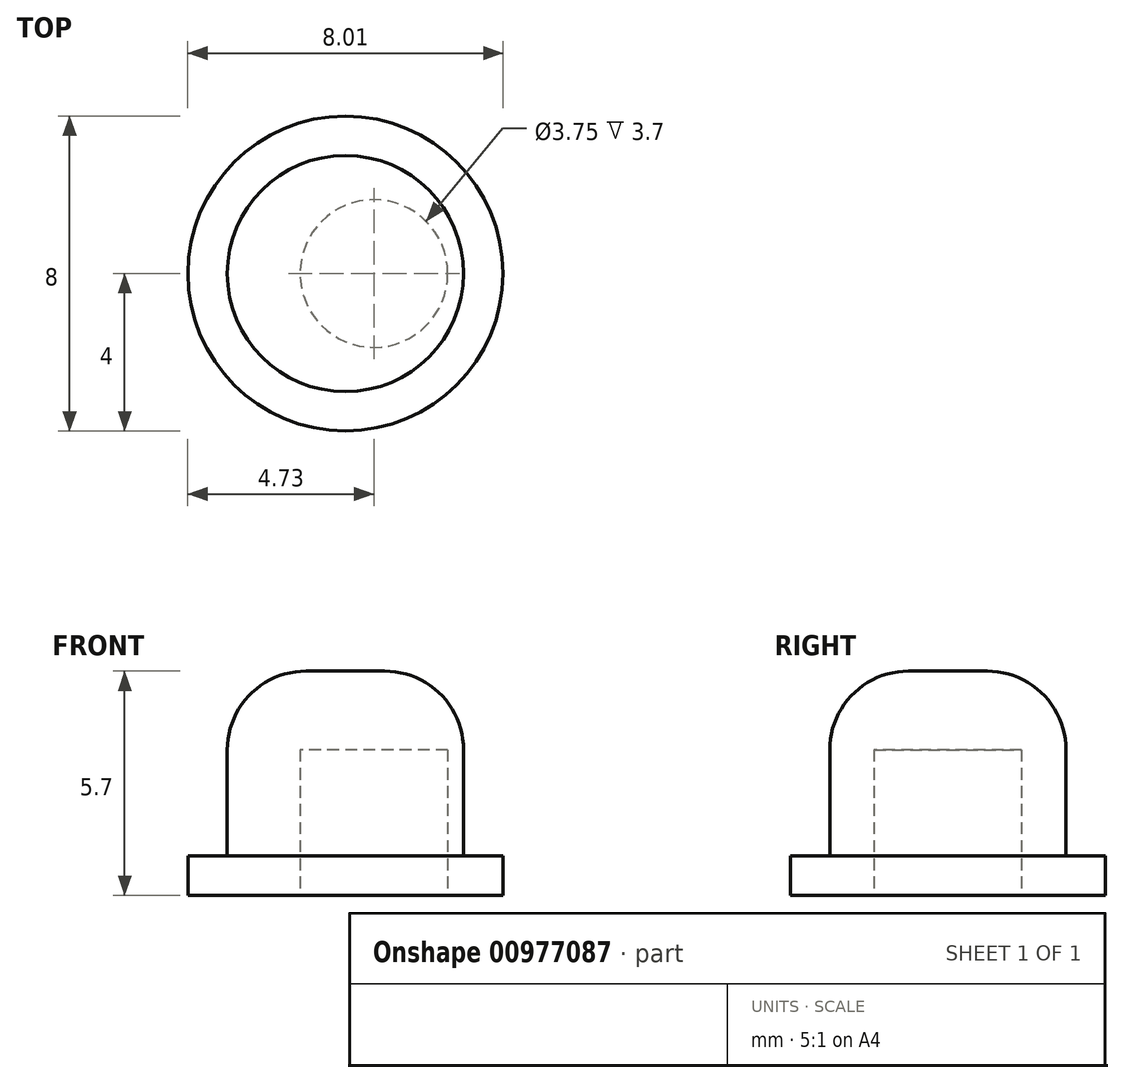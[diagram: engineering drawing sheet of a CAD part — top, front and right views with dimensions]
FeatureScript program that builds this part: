
annotation { "Feature Type Name" : "Feature", "Feature Type Description" : "" }
export const myFeature = defineFeature(function(context is Context, id is Id, definition is map)
    precondition{}
    {
        {
            var Q0;
            Q0=qCreatedBy(makeId("Top.planeOp"),FACE);
            var sketch = newSketch(context, id + "F0", { "sketchPlane" : qUnion([Q0])});
            skCircle(sketch, "E0", {"center": v(0, 0) * mm, "radius": 1.88 * mm});
            skCircle(sketch, "E1", {"center": v(-0.72, 0) * mm, "radius": 3 * mm});
            skCircle(sketch, "E2.0", {"center": v(-0.72, 0) * mm, "radius": 4 * mm});
            skSolve(sketch);
        }
        {
            var Q0;
            Q0 = qSketchRegion(id + "F0", true);
            extrude(context, id + "F1", {"entities" : qUnion([Q0]), "depth" : 1 * mm, "offsetDistance" : 25 * mm});
        }
        {
            var Q0;
            Q0=makeQuery(id+"F0.imprint","IMPRINT",FACE,{"disambiguationData":[TD([[makeQuery(id+"F0.imprint","IMPRINT",EDGE,{"derivedFrom":sQuery(id+"F0.wireOp",EDGE,"E0")}),-1.0]])]});
            extrude(context, id + "F2", {"entities" : qUnion([Q0]), "operationType" : NewBodyOperationType.ADD, "depth" : 3.7 * mm, "offsetDistance" : 25 * mm});
        }
        {
            var Q0;
            Q0=makeQuery(id+"F2.opExtrude","CAP_FACE",FACE,{"disambiguationData":[OSD([sQuery(id+"F0.wireOp",EDGE,"E0"),sQuery(id+"F0.wireOp",EDGE,"E1")])],"isStart":false});
            var sketch = newSketch(context, id + "F3", { "sketchPlane" : qUnion([Q0])});
            skCircle(sketch, "E3.0", {"center": v(-0.72, 0) * mm, "radius": 3 * mm});
            skSolve(sketch);
        }
        {
            var Q0;
            Q0=makeQuery(id+"F3.imprint","IMPRINT",FACE,{"disambiguationData":[TD([[makeQuery(id+"F3.imprint","IMPRINT",EDGE,{"derivedFrom":makeQuery(id+"F2.opExtrude","CAP_EDGE",EDGE,{"disambiguationData":[OSD([sQuery(id+"F0.wireOp",EDGE,"E0")])],"isStart":false})}),1.0]])]});
            var Q1;
            Q1=makeQuery(id+"F3.imprint","IMPRINT",FACE,{"disambiguationData":[TD([[makeQuery(id+"F3.imprint","IMPRINT",EDGE,{"derivedFrom":sQuery(id+"F3.wireOp",EDGE,"E3.0")}),1.0]])]});
            extrude(context, id + "F4", {"entities" : qUnion([Q0, Q1]), "operationType" : NewBodyOperationType.ADD, "depth" : 2 * mm, "offsetDistance" : 25 * mm});
        }
        {
            var Q0;
            Q0=makeQuery(id+"F4.opExtrude","CAP_EDGE",EDGE,{"disambiguationData":[OSD([sQuery(id+"F3.wireOp",EDGE,"E3.0")])],"isStart":false});
            fillet(context, id + "F5", {"entities" : qUnion([Q0]), "radius" : 2 * mm, "tangentPropagation" : true, "allowEdgeOverflow" : false});
        }
    });
